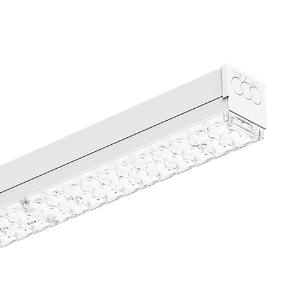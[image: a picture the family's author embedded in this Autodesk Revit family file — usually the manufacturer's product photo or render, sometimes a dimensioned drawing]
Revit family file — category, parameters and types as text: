
# Revit family: 3f_filippi_-_3f_zeta_l_3f_filippi_-_10894_-_3f_zeta_l_15_led_l605
name_source: partatom
category: Lighting Fixtures
units: mm (PartAtom-declared; Revit-internal decimal feet)

## family parameters
Cut with Voids When Loaded = No
Host = Face
Light Source = No
Part Type = Normal
Room Calculation Point = No
Round Connector Dimension = Use Diameter
Shared = No

## types (1)
- 3F Filippi - 3F Zeta L (1 x LED, 2749 lm, 17 W, 4000 K)
    Apparent Load = 17 VA
    Approval mark = CE
    CIE Flux Codes = 61 95 99 99 100
    Color Rendering = 80
    Color Temperature = 4000 K
    Control Gear = Electronic ballast
    Default Elevation = 1800 mm
    Description = ILLUMINOTECHNICAL
Luminous efficiency 100% (DLOR 99%, ULOR 1%).
Initial luminous flux of the luminaire 2749 lm.
Direct symmetric distribution.
Installation Interdistance Transv.D = 1.39 x hu - Long.D = 1.43 x hu.
Tabular UGR (CIE 117 - 4H-8H; S=0.25H; 70/50/20): RUG 21.6 - 22.3.
Beam angle: 102° - 103°.
Luminous efficacy 162 lm/W.
Lifetime (L93/B10): 30000 h. (tq+25°C)
Lifetime (L90/B10): 50000 h. (tq+25°C)
Lifetime (L85/B10): 80000 h. (tq+25°C)
Lifetime (L80/B10): 100000 h. (tq+25°C)
Sudden decreased luminous flux after 50000 hours: 0% (C0).
Photobiological safety in compliance with IEC/TR 62778: RG0 risk exempt, (IEC 62471).
In compliance with IEC/EN 62722-2-1 - IEC/EN 62717 standards.

SOURCE
Linear LED module 15W/840.
Energy efficiency class (UE 2019/2020 - UE 2019/2015): D.
CIE 13.3 Colour rendering index: CRI >80 (R9 <50%).
IES TM-30 Fidelity Index: Rf = 84 Rg = 95.
CCT nominal colour temperature 4000 K.
Colour initial tolerance (MacAdam): SDCM 3.

MECHANICAL
Housing in hot-galvanised steel, painted in white polyester, obtained through rolling process.
Light unit in hot-galvanised steel, painted in white polyester base with fixing springs and retractable safety hooks in stainless steel.
Lenses for wide distribution, in transparent methacrylate (PMMA) with external flat surface.
End caps in white polycarbonate.
Pair of stainless steel sliding brackets with sliding block screws.
Luminaire with limited surface temperature. - D - (EN 60598-2-24)
Dimensions: 605x62 mm, height 65 mm. Weight 2.32 kg.
IP40 protection degree.
Mechanical strength to impacts IK06 (1 joule).
Glow-wire test resistance 650°C.

ELECTRICAL
Halogen Free electronic wiring 230V-50/60Hz, power factor 0.85, THD <25%, constant output current, class I, 1 driver.
Power of the luminaire 17 W.
ENEC - CE.
SAFE FLICKER: PstLM=<1 and SVM=<0.4 (IEC TR 61547-1 and IEC TR 63158), to ensure a more comfortable and safe light.
Luminaire compliant with EN 60598-2-22 for power supply from a centralised emergency system CPSS (Central Power Supply System), not incorporated in the luminaire - high risk areas excluded. The default power and flux are 100% in AC and 100% in DC.
Ambient temperature from 0°C to +45°C.
Temperature class T6 max 85°C.
Relative humidity UR: <85%.

INSTALLATION
Ceiling / Suspended / Wall.
All accessories dedicated to this product are available on the Catalog and on our website www.3F-Filippi.com.

APPLICATIONS
Suitable product for food production plants (HACCP), IFS (Food Version 6), BRC (GSFS Food Version 7).
In commercial environments, exhibition areas, shops and stores.

WARNING
Luminaire designed for disposal/recycling at end-of-life.
Replaceable (LED only) light source by a professional. Replaceable control gear by a professional.
    Height = 65 mm
    Lamp = 1 x LED
    Lamp Light Flux = 2749 lm
    Lamp Power = 17 W
    Lamp count = 1
    Length = 605 mm
    Lifetime = 50000 h
    Luminous efficacy = 162 lm/W
    Manufacturer = 3F Filippi
    ModVariant = No
    Model = 3F Filippi - 10894 - 3F Zeta L 15 LED L605
    Mounting Place = Ceiling
    Mounting Type = Pendant
    Number of Poles = 1
    OnlyDefault = Yes
    Power Factor = 1
    Product Name = 3F Filippi - 3F Zeta L
    Product group = pendant luminaire
    ProductGroupID = 9
    Protection Class = Protection class I
    Protection Degree = IP 40
    RLX_Detail_Level = 1
    RLX_Emergency_Light_Flux = 0 lm
    RLX_Emergency_Type = 0
    RLX_Emergency_Type_DB = No
    RlxData = <blob elided: 37357 chars, md5=7945e0fe>
    Socket = socket
    Standby Power = 0 W
    System Light Flux = 2749 lm
    System Power = 17 W
    Type Comments = Product without accessories
    Type Image = 3ffilippi_3f_zeta_l.jpg
    URL = http://relux.com
    VarID = ---
    Voltage = 0 V
    Weight = 0.00 kg
    Width = 62 mm  [stored 0.203412 ft]

note: [stored X ft] marks values corroborated as IEEE doubles in the binary element streams (Revit-internal decimal feet)

## geometry (parser evidence)
native form markers: Blend x4, Sweep x10
no freeform markers — native parametric forms only
